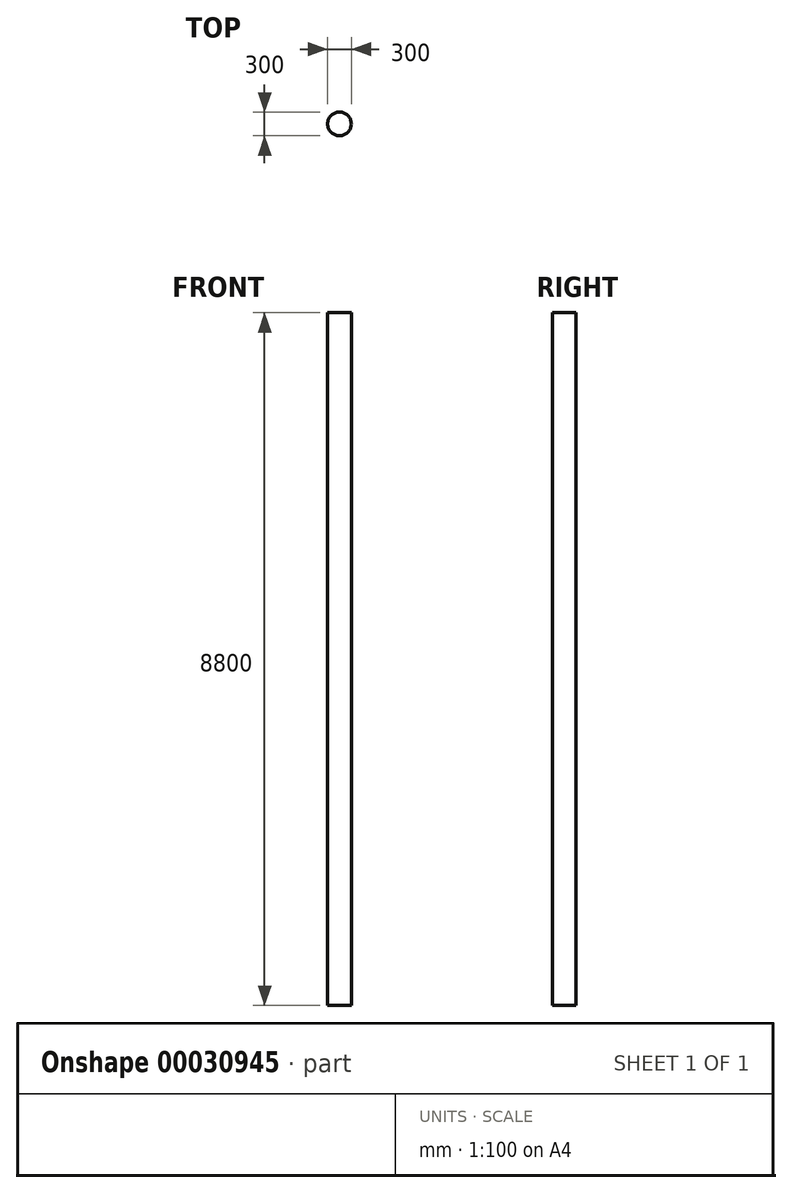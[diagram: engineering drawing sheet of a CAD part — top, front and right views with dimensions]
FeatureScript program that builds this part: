
annotation { "Feature Type Name" : "Feature", "Feature Type Description" : "" }
export const myFeature = defineFeature(function(context is Context, id is Id, definition is map)
    precondition{}
    {
        {
            var Q0;
            Q0=qCreatedBy(makeId("Top.planeOp"),FACE);
            var sketch = newSketch(context, id + "F0", { "sketchPlane" : qUnion([Q0])});
            skCircle(sketch, "E0", {"center": v(0, 0) * mm, "radius": 150 * mm});
            skSolve(sketch);
        }
        {
            var Q0;
            Q0 = qSketchRegion(id + "F0", true);
            extrude(context, id + "F1", {"entities" : qUnion([Q0]), "depth" : 8800 * mm});
        }
    });
